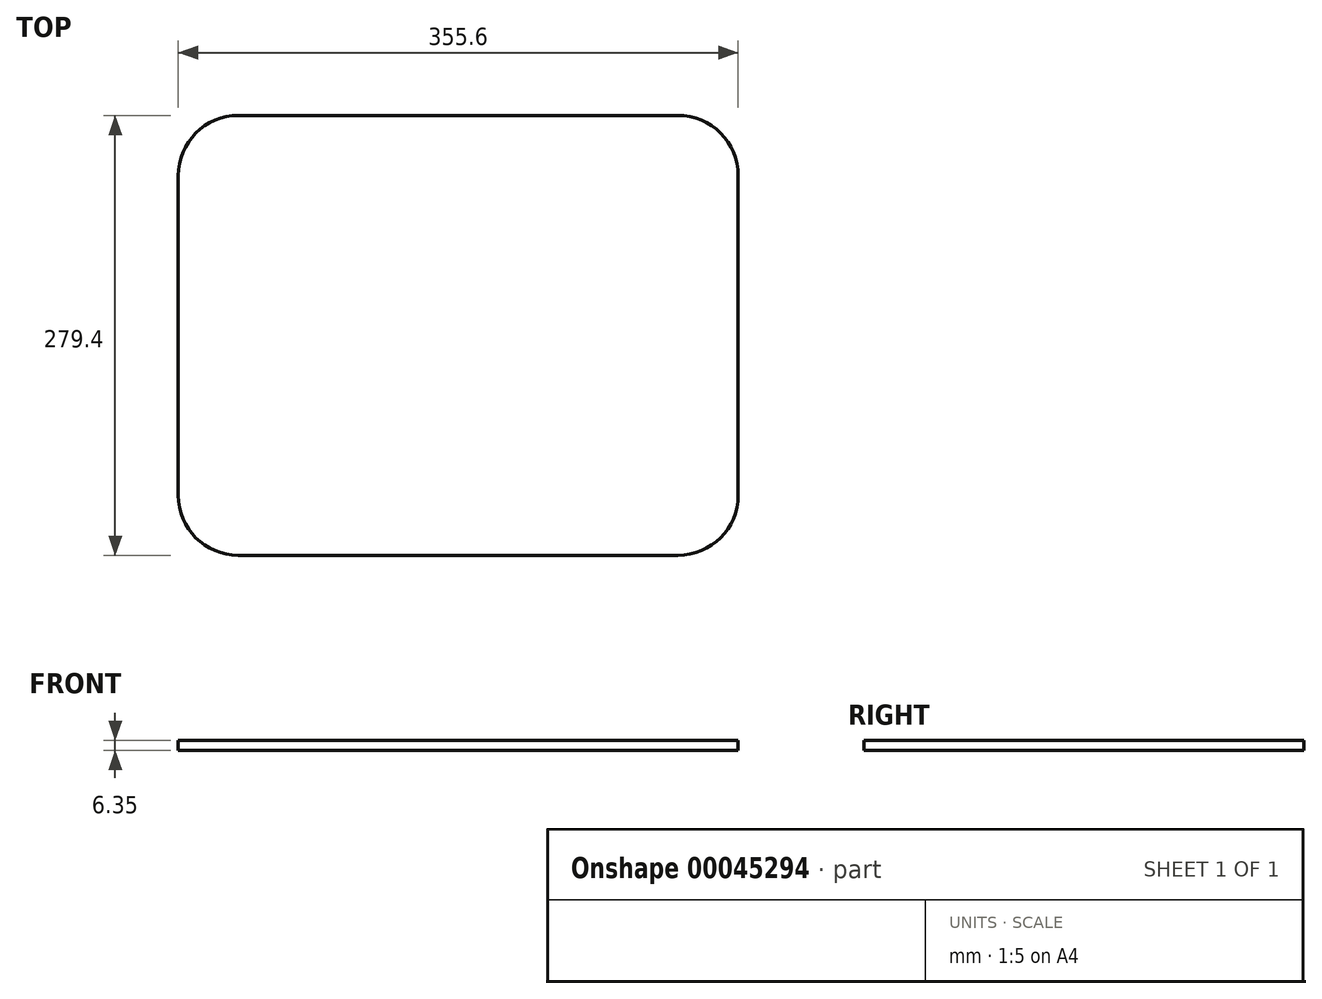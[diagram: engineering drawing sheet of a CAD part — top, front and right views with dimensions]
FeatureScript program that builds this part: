
annotation { "Feature Type Name" : "Feature", "Feature Type Description" : "" }
export const myFeature = defineFeature(function(context is Context, id is Id, definition is map)
    precondition{}
    {
        {
            var Q0;
            Q0=qCreatedBy(makeId("Top.planeOp"),FACE);
            var sketch = newSketch(context, id + "F0", { "sketchPlane" : qUnion([Q0])});
            skLineSegment(sketch, "E0.bottom", {"start": v(38.1, 0) * mm, "end": v(317.5, 0) * mm});
            skLineSegment(sketch, "E0.top", {"start": v(38.1, 279.4) * mm, "end": v(317.5, 279.4) * mm});
            skLineSegment(sketch, "E0.left", {"start": v(0, 38.1) * mm, "end": v(0, 241.3) * mm});
            skLineSegment(sketch, "E0.right", {"start": v(355.6, 38.1) * mm, "end": v(355.6, 241.3) * mm});
            skPoint(sketch, "E1.visualSharp", {"position": v(0, 279.4) * mm});
            skArc(sketch, "E1.filletArc", {"start": v(38.1, 279.4) * mm, "mid": v(11.16, 268.24) * mm, "end": v(0, 241.3) * mm});
            skPoint(sketch, "E2.visualSharp", {"position": v(355.6, 279.4) * mm});
            skArc(sketch, "E2.filletArc", {"start": v(355.6, 241.3) * mm, "mid": v(344.44, 268.24) * mm, "end": v(317.5, 279.4) * mm});
            skPoint(sketch, "E3.visualSharp", {"position": v(355.6, 0) * mm});
            skArc(sketch, "E3.filletArc", {"start": v(317.5, 0) * mm, "mid": v(344.44, 11.16) * mm, "end": v(355.6, 38.1) * mm});
            skPoint(sketch, "E4.visualSharp", {"position": v(0, 0) * mm});
            skArc(sketch, "E4.filletArc", {"start": v(0, 38.1) * mm, "mid": v(11.16, 11.16) * mm, "end": v(38.1, 0) * mm});
            skSolve(sketch);
        }
        {
            var Q0;
            Q0=makeQuery(id+"F0.imprint","IMPRINT",FACE,{"disambiguationData":[TD([[makeQuery(id+"F0.imprint","IMPRINT",EDGE,{"derivedFrom":sQuery(id+"F0.wireOp",EDGE,"E0.bottom")}),1.0]])]});
            extrude(context, id + "F1", {"entities" : qUnion([Q0]), "depth" : 6.35 * mm});
        }
    });
